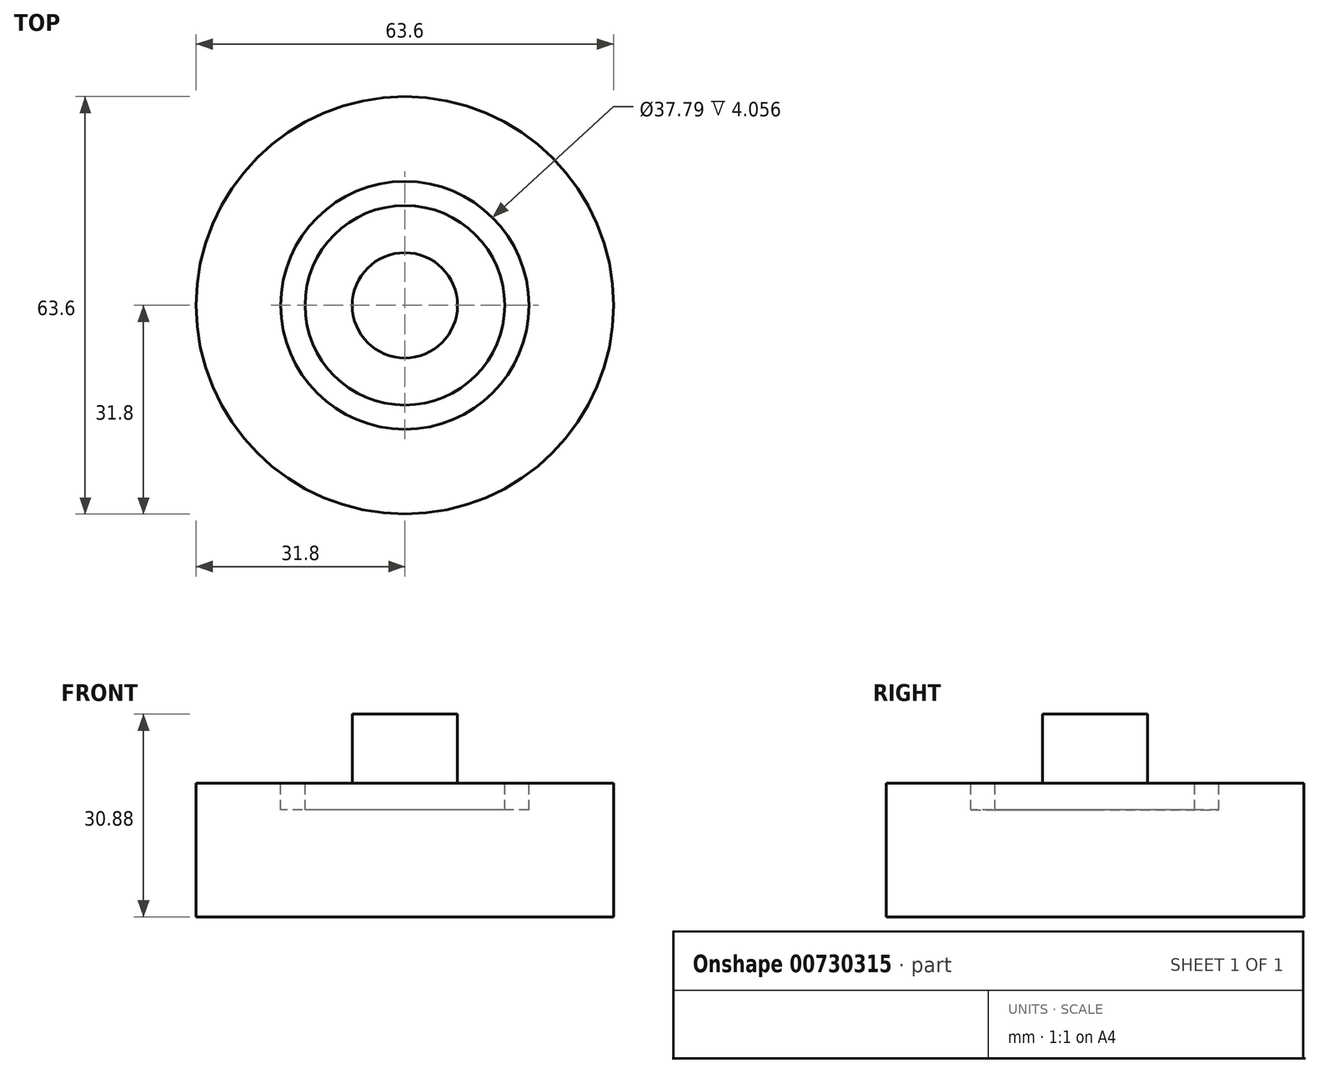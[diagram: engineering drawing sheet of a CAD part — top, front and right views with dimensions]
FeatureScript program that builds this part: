
annotation { "Feature Type Name" : "Feature", "Feature Type Description" : "" }
export const myFeature = defineFeature(function(context is Context, id is Id, definition is map)
    precondition{}
    {
        {
            var Q0;
            Q0=qCreatedBy(makeId("Front.planeOp"),FACE);
            var sketch = newSketch(context, id + "F0", { "sketchPlane" : qUnion([Q0])});
            skLineSegment(sketch, "E0", {"start": v(0, 0) * mm, "end": v(31.8, 0) * mm});
            skLineSegment(sketch, "E1", {"start": v(31.8, 0) * mm, "end": v(31.8, 20.37) * mm});
            skLineSegment(sketch, "E2", {"start": v(31.8, 20.37) * mm, "end": v(18.9, 20.37) * mm});
            skLineSegment(sketch, "E3", {"start": v(18.9, 20.37) * mm, "end": v(18.9, 16.32) * mm});
            skLineSegment(sketch, "E4", {"start": v(18.9, 16.32) * mm, "end": v(15.2, 16.32) * mm});
            skLineSegment(sketch, "E5", {"start": v(15.2, 16.32) * mm, "end": v(15.2, 20.37) * mm});
            skLineSegment(sketch, "E6", {"start": v(15.2, 20.37) * mm, "end": v(8.02, 20.37) * mm});
            skLineSegment(sketch, "E7", {"start": v(8.02, 20.37) * mm, "end": v(8.02, 30.88) * mm});
            skLineSegment(sketch, "E8", {"start": v(8.02, 30.88) * mm, "end": v(0, 30.88) * mm});
            skLineSegment(sketch, "E9", {"start": v(0, 30.88) * mm, "end": v(0, 0) * mm});
            skSolve(sketch);
        }
        {
            var Q0;
            Q0 = qSketchRegion(id + "F0", true);
            var Q1;
            Q1=sQuery(id+"F0.wireOp",EDGE,"E9");
            revolve(context, id + "F1", {"surfaceOperationType" : NewSurfaceOperationType.NEW, "entities" : qUnion([Q0]), "axis" : qUnion([Q1]), "revolveType" : RevolveType.FULL});
        }
    });
